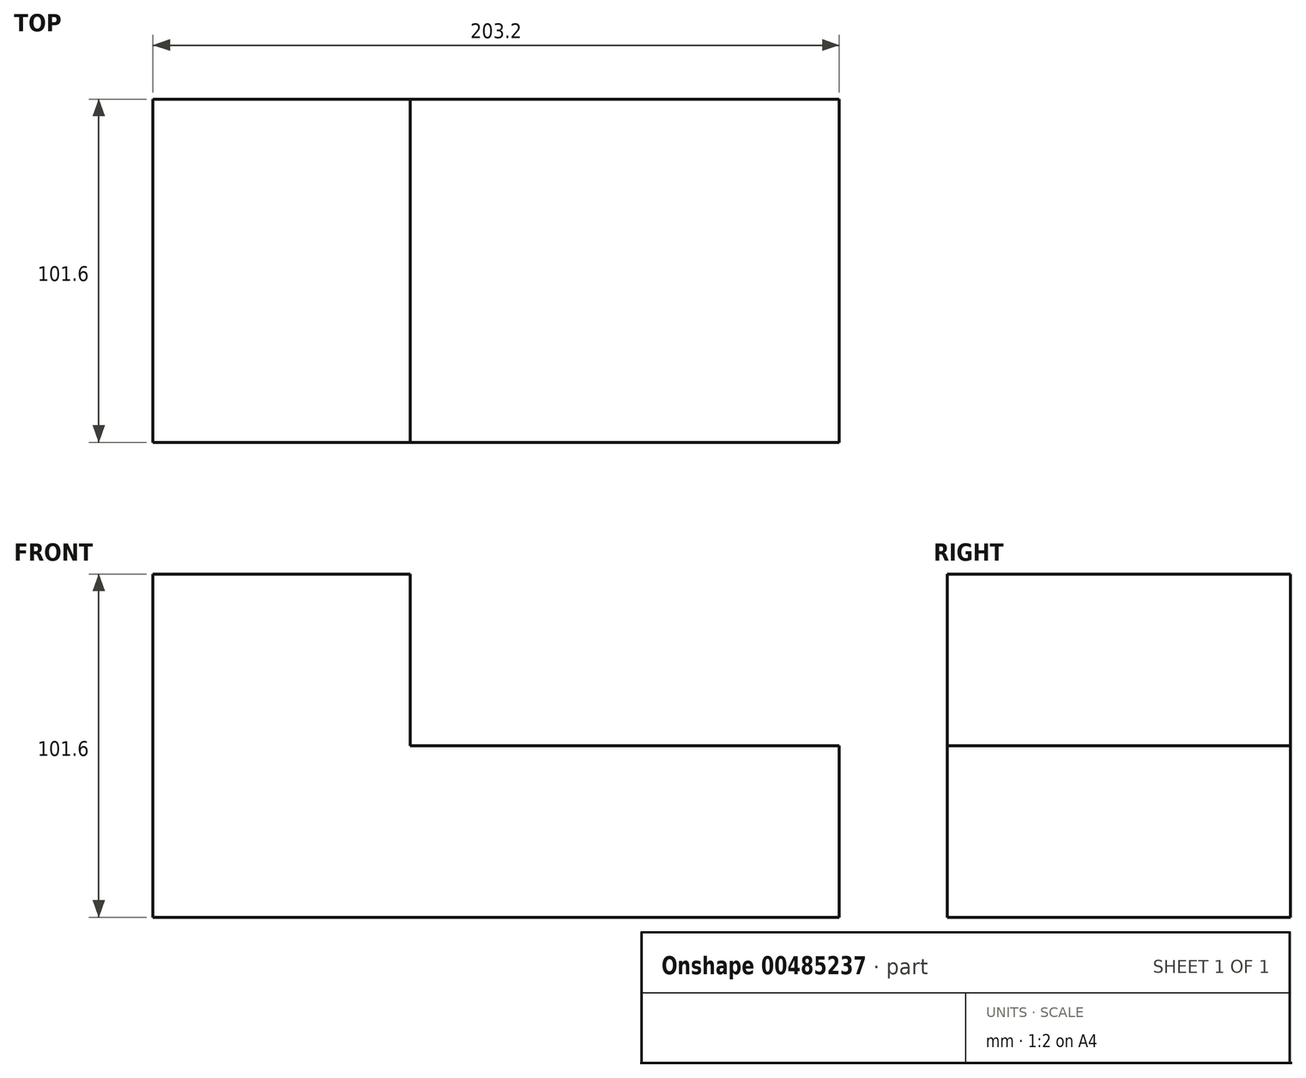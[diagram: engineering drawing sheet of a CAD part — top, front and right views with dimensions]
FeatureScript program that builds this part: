
annotation { "Feature Type Name" : "Feature", "Feature Type Description" : "" }
export const myFeature = defineFeature(function(context is Context, id is Id, definition is map)
    precondition{}
    {
        {
            var Q0;
            Q0=qCreatedBy(makeId("Front.planeOp"),FACE);
            var sketch = newSketch(context, id + "F0", { "sketchPlane" : qUnion([Q0])});
            skLineSegment(sketch, "E0.bottom", {"start": v(127, 0) * mm, "end": v(-76.2, 0) * mm});
            skLineSegment(sketch, "E0.top", {"start": v(127, -50.8) * mm, "end": v(-76.2, -50.8) * mm});
            skLineSegment(sketch, "E0.left", {"start": v(127, 0) * mm, "end": v(127, -50.8) * mm});
            skLineSegment(sketch, "E0.right", {"start": v(-76.2, 0) * mm, "end": v(-76.2, -50.8) * mm});
            skLineSegment(sketch, "E1.bottom", {"start": v(0, 0) * mm, "end": v(-76.2, 0) * mm});
            skLineSegment(sketch, "E1.top", {"start": v(0, 50.8) * mm, "end": v(-76.2, 50.8) * mm});
            skLineSegment(sketch, "E1.left", {"start": v(0, 0) * mm, "end": v(0, 50.8) * mm});
            skLineSegment(sketch, "E1.right", {"start": v(-76.2, 0) * mm, "end": v(-76.2, 50.8) * mm});
            skSolve(sketch);
        }
        {
            var Q0;
            Q0 = qSketchRegion(id + "F0", true);
            extrude(context, id + "F1", {"entities" : qUnion([Q0]), "depth" : 101.6 * mm});
        }
    });
